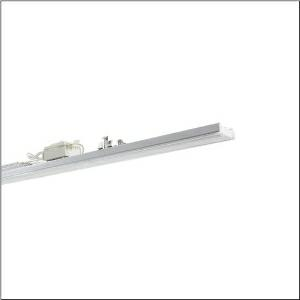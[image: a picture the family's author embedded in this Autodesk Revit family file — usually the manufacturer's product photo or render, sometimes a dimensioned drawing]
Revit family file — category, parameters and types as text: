
# Revit family: licross_11_recessed_mo_51tl12dv4fxg3s
name_source: partatom
category: Lighting Fixtures
units: mm (PartAtom-declared; Revit-internal decimal feet)

## family parameters
Cut with Voids When Loaded = No
Host = Face
Light Source = No
Part Type = Normal
Room Calculation Point = No
Round Connector Dimension = Use Diameter
Shared = No

## types (1)
- --- (1 x LED, 1010 lm, 5.5 W, 4000K)
    Apparent Load = 6 VA
    CIE Flux Codes = 67 92 99 100 100
    Color Rendering = 80
    Color Temperature = 4000K
    Default Elevation = 1800 mm
    Description = Licross 11 Recessed MO, luminaire insert, of sheet steel, coil coated, white, length: 2.250mm, width: 66mm, height: 67mm, LED rated luminous flux: 15.360lm, light colour: 840, SDCM (Standard Deviation of Colour Matching)MacAdam ≤ 2 SDCM (initial), control gear: DALI 2 (for two DALI lines), with plug, 6-pole, with phase selection, for trunking rail, 14-core, mains connection: 220..240V, AC, 50/60Hz, rated input power: 88W, for trunking rail, 14-core, internal wiring halogen-free, for emergency light function, converter,control gear: single battery element, battery: LiFePO4, 9Ah, primary optical cover: cover, of PMMA, light emission: direct distribution, primary light characteristic: symmetric, protection rating (complete): IP40, insulation class (complete): insulation class I (protective earthing), certification: CE, UKCA, protection symbol: D if used in an environment without relevant dust loads with corresponding accessories, impact resistance: IK06, permissible ambient temperature for indoor applications: +5..+35°C, standard: EN 60598-2-22, LABS conformity tested according to VDMA 24364:2018-05, reducing of maximum allowable ambient temperature of 5°C with ceiling mounting, corresponds to IFS (International Featured Standards) requirements for safety and quality in the food industry, The light source and the operating device comply with the requirements of the Ecodesign Regulation (EU) 2019/2020 and are replaceable in accordance with this regulation, packaging unit: 1 piece
    Height = 58 mm
    Lamp = 1 x LED
    Lamp Light Flux = 1010 lm
    Lamp Power = 5.5 W
    Lamp count = 1
    Length = 2250 mm
    Luminous efficacy = 184 lm/W
    Manufacturer = Siteco
    ModVariant = No
    Model = 51TL12DV4FXG3S
    Mounting Place = Ceiling
    Mounting Type = Pendant
    Number of Poles = 1
    OnlyDefault = Yes
    Power Factor = 1
    Product Name = Licross 11 Recessed MO
    Product group = luminaire insert | ceiling pendant
    ProductGroupID = 901
    Protection Class = Protection class I
    Protection Degree = IP 40
    RLX_Detail_Level = 1
    RLX_Emergency_Light_Flux = 0 lm
    RLX_Emergency_Type = 0
    RLX_Emergency_Type_DB = No
    RlxData = <blob elided: 29849 chars, md5=7b49e147>
    Socket = socket
    Standby Power = 0 W
    System Light Flux = 1010 lm
    System Power = 6 W
    Type Comments = : emergency light operation: 3 h
    Type Image = l_1296930.jpg
    URL = http://relux.com
    VarID = @adj_090025
    Voltage = 0 V
    Weight = 0.00 kg
    Width = 66 mm

## geometry (parser evidence)
native form markers: Blend x4, Sweep x8
no freeform markers — native parametric forms only
